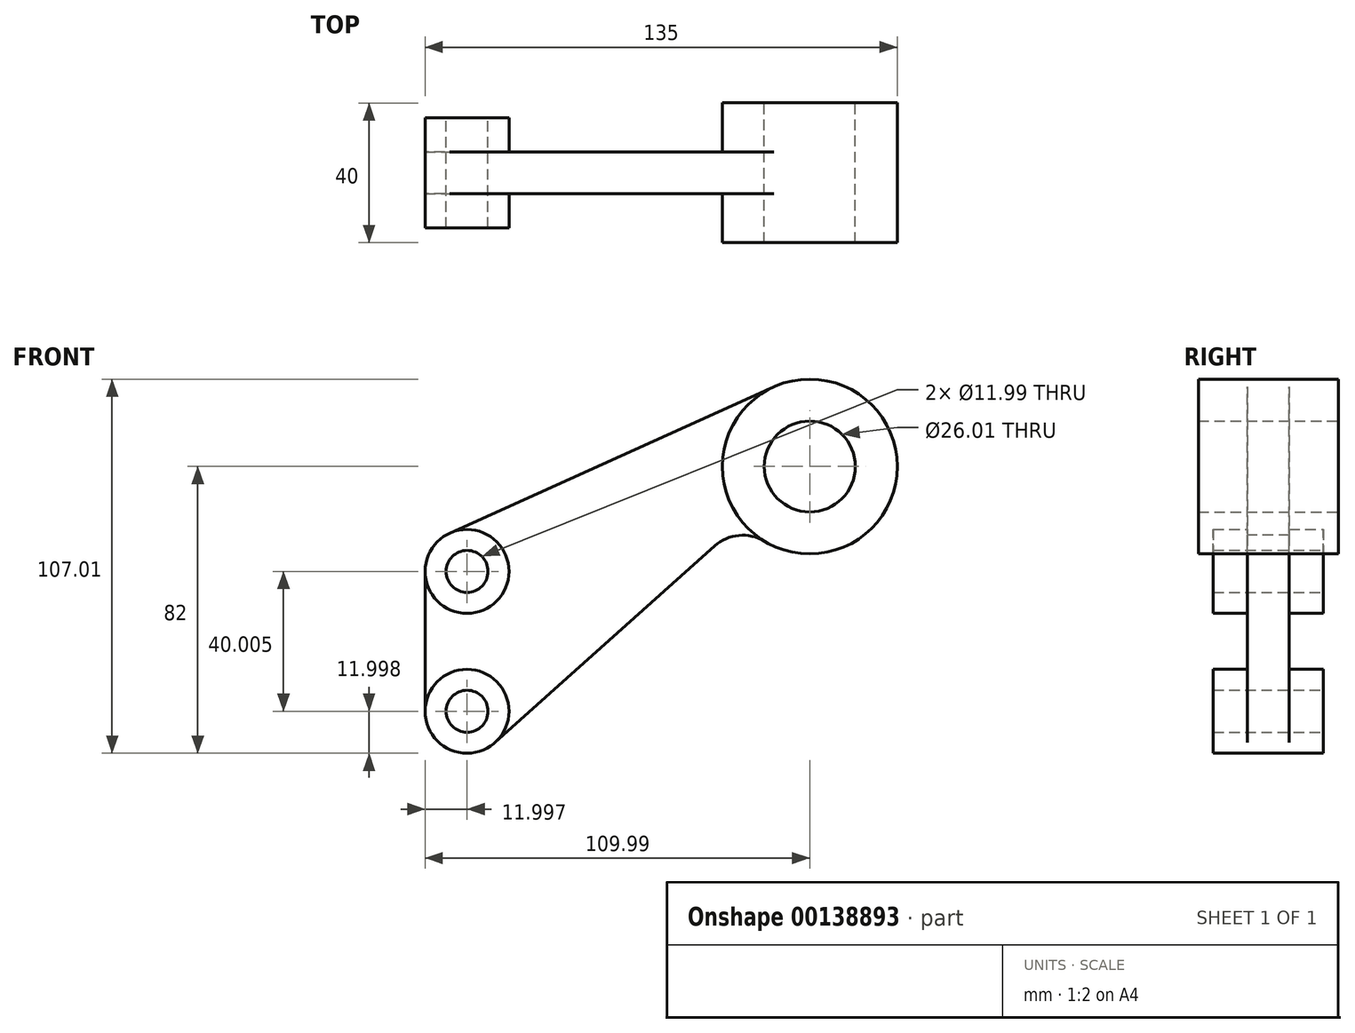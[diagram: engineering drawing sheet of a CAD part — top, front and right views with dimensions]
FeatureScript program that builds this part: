
annotation { "Feature Type Name" : "Feature", "Feature Type Description" : "" }
export const myFeature = defineFeature(function(context is Context, id is Id, definition is map)
    precondition{}
    {
        {
            var Q0;
            Q0=qCreatedBy(makeId("Front.planeOp"),FACE);
            var sketch = newSketch(context, id + "F0", { "sketchPlane" : qUnion([Q0])});
            skCircle(sketch, "E0", {"center": v(0, 0) * mm, "radius": 13 * mm});
            skCircle(sketch, "E1", {"center": v(0, 0) * mm, "radius": 25 * mm});
            skCircle(sketch, "E2", {"center": v(-98, -30) * mm, "radius": 6 * mm});
            skCircle(sketch, "E3", {"center": v(-98, -70) * mm, "radius": 6 * mm});
            skCircle(sketch, "E4", {"center": v(-98, -30) * mm, "radius": 12 * mm});
            skCircle(sketch, "E5", {"center": v(-98, -70) * mm, "radius": 12 * mm});
            skLineSegment(sketch, "E6", {"start": v(-102.93, -19.06) * mm, "end": v(-10.3, 22.79) * mm});
            skLineSegment(sketch, "E7", {"start": v(-110, -30) * mm, "end": v(-110, -70) * mm});
            skArc(sketch, "E8", {"start": v(-12.95, -21.4) * mm, "mid": v(-20.27, -19.71) * mm, "end": v(-27.15, -22.71) * mm});
            skLineSegment(sketch, "E9", {"start": v(-90, -78.95) * mm, "end": v(-27.15, -22.71) * mm});
            skSolve(sketch);
        }
        {
            var Q0;
            {var subQ0=sQuery(id+"F0.wireOp",EDGE,"E6");Q0=makeQuery(id+"F0.imprint","IMPRINT",FACE,{"disambiguationData":[TD([[makeQuery(id+"F0.imprint","IMPRINT",EDGE,{"derivedFrom":subQ0}),-1.0]])]});}
            extrude(context, id + "F1", {"entities" : qUnion([Q0]), "endBound" : BoundingType.SYMMETRIC, "oppositeDirection" : true, "depth" : 12 * mm});
        }
        {
            var Q0;
            Q0=makeQuery(id+"F0.imprint","IMPRINT",FACE,{"disambiguationData":[TD([[makeQuery(id+"F0.imprint","IMPRINT",EDGE,{"derivedFrom":sQuery(id+"F0.wireOp",EDGE,"E2")}),-1.0]])]});
            var Q1;
            Q1=makeQuery(id+"F0.imprint","IMPRINT",FACE,{"disambiguationData":[TD([[makeQuery(id+"F0.imprint","IMPRINT",EDGE,{"derivedFrom":sQuery(id+"F0.wireOp",EDGE,"E3")}),-1.0]])]});
            extrude(context, id + "F2", {"entities" : qUnion([Q0, Q1]), "operationType" : NewBodyOperationType.ADD, "endBound" : BoundingType.SYMMETRIC, "depth" : 31.5 * mm});
        }
        {
            var Q0;
            Q0=makeQuery(id+"F0.imprint","IMPRINT",FACE,{"disambiguationData":[TD([[makeQuery(id+"F0.imprint","IMPRINT",EDGE,{"derivedFrom":sQuery(id+"F0.wireOp",EDGE,"E0")}),-1.0]])]});
            extrude(context, id + "F3", {"entities" : qUnion([Q0]), "operationType" : NewBodyOperationType.ADD, "endBound" : BoundingType.SYMMETRIC, "depth" : 40 * mm});
        }
    });
